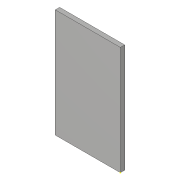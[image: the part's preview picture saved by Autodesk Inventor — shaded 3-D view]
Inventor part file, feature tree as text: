
AUTODESK INVENTOR PART (.ipt)
format: ipt  version: 2018 (Build 220112000, 112)  size: 87,552 bytes
history: native  units: in
note: dims shown in document units (in); Inventor stores cm internally (conversion verified against a paired STEP export)
features: sketch x1
ambient origin geometry x8: Origin, YZ Plane, XZ Plane, XY Plane, X Axis, Y Axis, Z Axis, Center Point
bodies: Solid1 (feature_tree), Body1 (feature_tree)
feature tree (1):
  sketch  "Sketch1"
